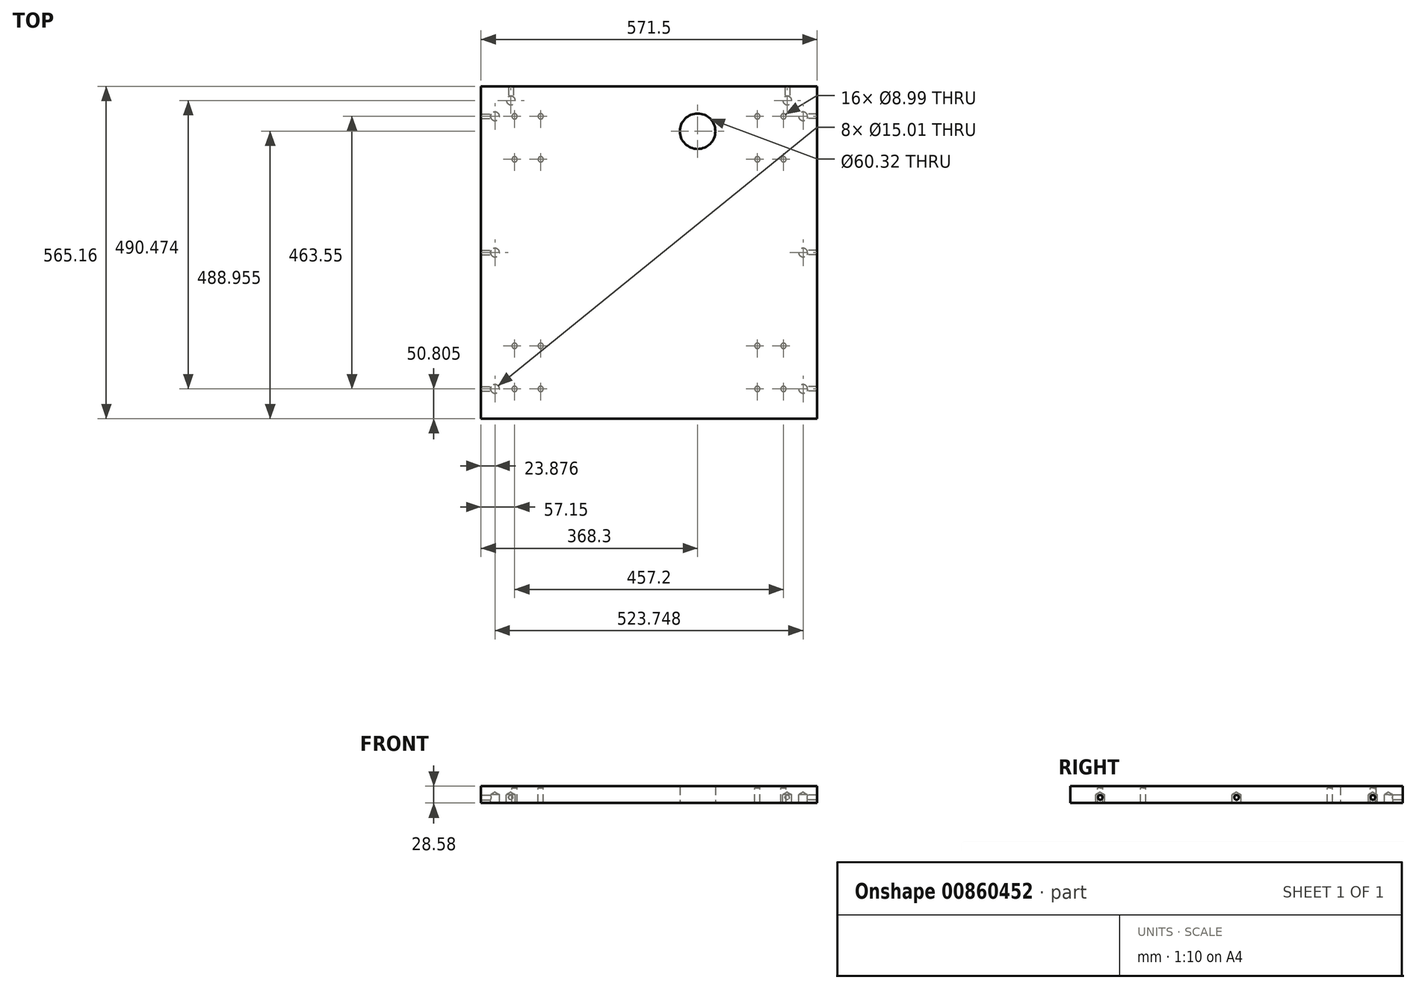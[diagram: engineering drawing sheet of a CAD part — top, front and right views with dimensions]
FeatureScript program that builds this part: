
annotation { "Feature Type Name" : "Feature", "Feature Type Description" : "" }
export const myFeature = defineFeature(function(context is Context, id is Id, definition is map)
    precondition{}
    {
        {
            var Q0;
            Q0=qCreatedBy(makeId("Top.planeOp"),FACE);
            var sketch = newSketch(context, id + "F0", { "sketchPlane" : qUnion([Q0])});
            skLineSegment(sketch, "E0.bottom", {"start": v(285.75, 282.58) * mm, "end": v(-285.75, 282.58) * mm});
            skLineSegment(sketch, "E0.top", {"start": v(285.75, -282.57) * mm, "end": v(-285.75, -282.58) * mm});
            skLineSegment(sketch, "E0.left", {"start": v(285.75, 282.58) * mm, "end": v(285.75, -282.57) * mm});
            skLineSegment(sketch, "E0.right", {"start": v(-285.75, 282.58) * mm, "end": v(-285.75, -282.58) * mm});
            skPoint(sketch, "E0.middle", {"position": v(0, 0) * mm});
            skCircle(sketch, "E1", {"center": v(82.55, 206.38) * mm, "radius": 30.16 * mm});
            skLineSegment(sketch, "E2", {"start": v(82.55, 206.38) * mm, "end": v(285.75, 206.38) * mm});
            skLineSegment(sketch, "E3", {"start": v(82.55, 206.38) * mm, "end": v(82.55, 282.58) * mm});
            skSolve(sketch);
        }
        {
            var Q0;
            Q0=makeQuery(id+"F0.imprint","IMPRINT",FACE,{"disambiguationData":[TD([[makeQuery(id+"F0.imprint","IMPRINT",EDGE,{"derivedFrom":sQuery(id+"F0.wireOp",EDGE,"E0.top")}),-1.0]])]});
            var Q1;
            {var subQ1=sQuery(id+"F0.wireOp",EDGE,"E0.left");var subQ7=sQuery(id+"F0.wireOp",EDGE,"E0.bottom");var subQ8=makeQuery(id+"F0.imprint","INTERSECT",VERTEX,{"derivedFrom":[subQ7,subQ1]});Q1=makeQuery(id+"F0.imprint","IMPRINT",FACE,{"disambiguationData":[TD([[makeQuery(id+"F0.imprint","IMPRINT",EDGE,{"disambiguationData":[TD([[subQ8,-1.0]])],"derivedFrom":subQ7}),1.0]])]});}
            extrude(context, id + "F1", {"entities" : qUnion([Q0, Q1]), "depth" : 28.57 * mm, "offsetDistance" : 25.4 * mm});
        }
        {
            var Q0;
            Q0=makeQuery(id+"F1.opExtrude","CAP_FACE",FACE,{"disambiguationData":[OSD([sQuery(id+"F0.wireOp",EDGE,"E0.bottom"),sQuery(id+"F0.wireOp",EDGE,"E0.top"),sQuery(id+"F0.wireOp",EDGE,"E0.left"),sQuery(id+"F0.wireOp",EDGE,"E0.right"),sQuery(id+"F0.wireOp",EDGE,"E1")])],"isStart":true});
            var sketch = newSketch(context, id + "F2", { "sketchPlane" : qUnion([Q0])});
            skLineSegment(sketch, "E4", {"start": v(-285.75, 282.58) * mm, "end": v(-261.87, 282.58) * mm});
            skLineSegment(sketch, "E5", {"start": v(-261.87, 282.58) * mm, "end": v(-261.87, 231.78) * mm});
            skLineSegment(sketch, "E6", {"start": v(-285.75, -282.57) * mm, "end": v(-261.87, -282.57) * mm});
            skLineSegment(sketch, "E7", {"start": v(-261.87, -282.57) * mm, "end": v(-261.87, -231.77) * mm});
            skLineSegment(sketch, "E8", {"start": v(-285.75, 0) * mm, "end": v(-261.87, 0) * mm});
            skLineSegment(sketch, "E9", {"start": v(285.75, 0) * mm, "end": v(261.87, 0) * mm});
            skLineSegment(sketch, "E10", {"start": v(285.75, 282.57) * mm, "end": v(261.87, 282.57) * mm});
            skLineSegment(sketch, "E11", {"start": v(261.87, 282.57) * mm, "end": v(261.87, 231.77) * mm});
            skLineSegment(sketch, "E12", {"start": v(285.75, -282.58) * mm, "end": v(261.87, -282.58) * mm});
            skLineSegment(sketch, "E13", {"start": v(261.87, -282.58) * mm, "end": v(261.87, -231.78) * mm});
            skPoint(sketch, "E14", {"position": v(-261.87, 231.78) * mm});
            skPoint(sketch, "E15", {"position": v(-261.87, 0) * mm});
            skPoint(sketch, "E16", {"position": v(-261.87, -231.77) * mm});
            skPoint(sketch, "E17", {"position": v(261.87, -231.78) * mm});
            skPoint(sketch, "E18", {"position": v(261.87, 0) * mm});
            skPoint(sketch, "E19", {"position": v(261.87, 231.77) * mm});
            skSolve(sketch);
        }
        {
            var Q0;
            Q0=sQuery(id+"F2.wireOp",VERTEX,"E14");
            var Q1;
            Q1=sQuery(id+"F2.wireOp",VERTEX,"E19");
            var Q2;
            Q2=sQuery(id+"F2.wireOp",VERTEX,"E15");
            var Q3;
            Q3=sQuery(id+"F2.wireOp",VERTEX,"E18");
            var Q4;
            Q4=sQuery(id+"F2.wireOp",VERTEX,"E17");
            var Q5;
            Q5=sQuery(id+"F2.wireOp",VERTEX,"E16");
            var Q6;
            Q6=makeQuery(id+"F1.opExtrude","SWEPT_BODY",BODY,{"disambiguationData":[OSD([sQuery(id+"F0.wireOp",EDGE,"E0.bottom"),sQuery(id+"F0.wireOp",EDGE,"E0.top"),sQuery(id+"F0.wireOp",EDGE,"E0.left"),sQuery(id+"F0.wireOp",EDGE,"E0.right"),sQuery(id+"F0.wireOp",EDGE,"E1")])]});
            hole(context, id + "F3", {"style" : HoleStyle.SIMPLE, "endStyle" : HoleEndStyle.BLIND, "holeDiameter" : 15 * mm, "majorDiameter" : 6.35 * mm, "holeDepth" : 14.22 * mm, "isTappedThrough" : true, "tappedDepth" : 12.7 * mm, "tapClearance" : 3, "locations" : qUnion([Q0, Q1, Q2, Q3, Q4, Q5]), "scope" : qUnion([Q6]), "startStyle" : HoleStartStyle.SKETCH});
        }
        {
            var Q0;
            Q0=makeQuery(id+"F1.opExtrude","SWEPT_FACE",FACE,{"disambiguationData":[OSD([sQuery(id+"F0.wireOp",EDGE,"E0.left")])]});
            var sketch = newSketch(context, id + "F4", { "sketchPlane" : qUnion([Q0])});
            skPoint(sketch, "E20", {"position": v(0, 9.52) * mm});
            skPoint(sketch, "E20.positionSnap0", {"position": v(0, 28.58) * mm});
            skPoint(sketch, "E21", {"position": v(-231.78, 9.53) * mm});
            skPoint(sketch, "E22", {"position": v(231.78, 9.52) * mm});
            skLineSegment(sketch, "E23", {"start": v(-231.78, 9.53) * mm, "end": v(-231.78, 0) * mm});
            skLineSegment(sketch, "E24", {"start": v(-282.58, 0) * mm, "end": v(-231.78, 0) * mm});
            skLineSegment(sketch, "E25", {"start": v(231.78, 9.52) * mm, "end": v(231.78, 0) * mm});
            skLineSegment(sketch, "E26", {"start": v(231.78, 0) * mm, "end": v(282.58, 0) * mm});
            skSolve(sketch);
        }
        {
            var Q0;
            Q0=sQuery(id+"F4.wireOp",VERTEX,"E21");
            var Q1;
            Q1=sQuery(id+"F4.wireOp",VERTEX,"E20");
            var Q2;
            Q2=sQuery(id+"F4.wireOp",VERTEX,"E22");
            var Q3;
            Q3=makeQuery(id+"F1.opExtrude","SWEPT_BODY",BODY,{"disambiguationData":[OSD([sQuery(id+"F0.wireOp",EDGE,"E0.bottom"),sQuery(id+"F0.wireOp",EDGE,"E0.top"),sQuery(id+"F0.wireOp",EDGE,"E0.left"),sQuery(id+"F0.wireOp",EDGE,"E0.right"),sQuery(id+"F0.wireOp",EDGE,"E1")])]});
            hole(context, id + "F5", {"style" : HoleStyle.SIMPLE, "endStyle" : HoleEndStyle.BLIND, "holeDiameter" : 8 * mm, "majorDiameter" : 6.35 * mm, "holeDepth" : 25.4 * mm, "isTappedThrough" : true, "tappedDepth" : 12.7 * mm, "tapClearance" : 3, "locations" : qUnion([Q0, Q1, Q2]), "scope" : qUnion([Q3]), "startStyle" : HoleStartStyle.SKETCH});
        }
        {
            var Q0;
            Q0=makeQuery(id+"F1.opExtrude","SWEPT_FACE",FACE,{"disambiguationData":[OSD([sQuery(id+"F0.wireOp",EDGE,"E0.right")])]});
            var sketch = newSketch(context, id + "F6", { "sketchPlane" : qUnion([Q0])});
            skPoint(sketch, "E27", {"position": v(-231.78, 9.53) * mm});
            skPoint(sketch, "E28", {"position": v(231.77, 9.52) * mm});
            skLineSegment(sketch, "E29", {"start": v(0, 0) * mm, "end": v(0, 9.53) * mm});
            skPoint(sketch, "E30", {"position": v(0, 9.53) * mm});
            skLineSegment(sketch, "E31", {"start": v(-231.78, 9.53) * mm, "end": v(-231.78, 0) * mm});
            skLineSegment(sketch, "E32", {"start": v(-231.78, 0) * mm, "end": v(-282.58, 0) * mm});
            skLineSegment(sketch, "E33", {"start": v(231.77, 9.52) * mm, "end": v(231.77, 0) * mm});
            skLineSegment(sketch, "E34", {"start": v(231.77, 0) * mm, "end": v(282.57, 0) * mm});
            skSolve(sketch);
        }
        {
            var Q0;
            Q0=sQuery(id+"F6.wireOp",VERTEX,"7JFDCdo1-Y3dr-wsHc-LP2G-7qkS5dpKQL4z.end");
            var Q1;
            Q1=sQuery(id+"F6.wireOp",VERTEX,"E30");
            var Q2;
            Q2=sQuery(id+"F6.wireOp",VERTEX,"E28");
            var Q3;
            Q3=sQuery(id+"F6.wireOp",VERTEX,"E27");
            var Q4;
            Q4=makeQuery(id+"F1.opExtrude","SWEPT_BODY",BODY,{"disambiguationData":[OSD([sQuery(id+"F0.wireOp",EDGE,"E0.bottom"),sQuery(id+"F0.wireOp",EDGE,"E0.top"),sQuery(id+"F0.wireOp",EDGE,"E0.left"),sQuery(id+"F0.wireOp",EDGE,"E0.right"),sQuery(id+"F0.wireOp",EDGE,"E1")])]});
            hole(context, id + "F7", {"style" : HoleStyle.SIMPLE, "endStyle" : HoleEndStyle.BLIND, "holeDiameter" : 8 * mm, "majorDiameter" : 6.35 * mm, "holeDepth" : 25.4 * mm, "isTappedThrough" : true, "tappedDepth" : 12.7 * mm, "tapClearance" : 3, "locations" : qUnion([Q0, Q1, Q2, Q3]), "scope" : qUnion([Q4]), "startStyle" : HoleStartStyle.SKETCH});
        }
        {
            var Q0;
            Q0=makeQuery(id+"F1.opExtrude","CAP_FACE",FACE,{"disambiguationData":[OSD([sQuery(id+"F0.wireOp",EDGE,"E0.bottom"),sQuery(id+"F0.wireOp",EDGE,"E0.top"),sQuery(id+"F0.wireOp",EDGE,"E0.left"),sQuery(id+"F0.wireOp",EDGE,"E0.right"),sQuery(id+"F0.wireOp",EDGE,"E1")])],"isStart":true});
            var sketch = newSketch(context, id + "F8", { "sketchPlane" : qUnion([Q0])});
            skLineSegment(sketch, "E35", {"start": v(-285.75, 282.58) * mm, "end": v(-228.6, 282.58) * mm});
            skLineSegment(sketch, "E36", {"start": v(-228.6, 282.58) * mm, "end": v(-228.6, 231.78) * mm});
            skLineSegment(sketch, "E37", {"start": v(285.75, 282.57) * mm, "end": v(228.6, 282.57) * mm});
            skLineSegment(sketch, "E38", {"start": v(228.6, 282.58) * mm, "end": v(228.6, 231.77) * mm});
            skLineSegment(sketch, "E39", {"start": v(-285.75, -282.57) * mm, "end": v(-228.6, -282.57) * mm});
            skLineSegment(sketch, "E40", {"start": v(-228.6, -282.57) * mm, "end": v(-228.6, -231.77) * mm});
            skLineSegment(sketch, "E41", {"start": v(285.75, -282.58) * mm, "end": v(228.6, -282.58) * mm});
            skLineSegment(sketch, "E42", {"start": v(228.6, -282.58) * mm, "end": v(228.6, -231.78) * mm});
            skPoint(sketch, "E43", {"position": v(-228.6, 231.78) * mm});
            skPoint(sketch, "E44", {"position": v(228.6, 231.77) * mm});
            skPoint(sketch, "E45", {"position": v(228.6, -231.78) * mm});
            skPoint(sketch, "E46", {"position": v(-228.6, -231.77) * mm});
            skLineSegment(sketch, "E47.bottom", {"start": v(-228.6, 231.78) * mm, "end": v(-184.15, 231.78) * mm});
            skLineSegment(sketch, "E47.top", {"start": v(-228.6, 158.62) * mm, "end": v(-184.15, 158.62) * mm});
            skLineSegment(sketch, "E47.left", {"start": v(-228.6, 231.78) * mm, "end": v(-228.6, 158.62) * mm});
            skLineSegment(sketch, "E47.right", {"start": v(-184.15, 231.78) * mm, "end": v(-184.15, 158.62) * mm});
            skLineSegment(sketch, "E48.bottom", {"start": v(228.6, 231.77) * mm, "end": v(184.15, 231.77) * mm});
            skLineSegment(sketch, "E48.top", {"start": v(228.6, 158.62) * mm, "end": v(184.15, 158.62) * mm});
            skLineSegment(sketch, "E48.left", {"start": v(228.6, 231.77) * mm, "end": v(228.6, 158.62) * mm});
            skLineSegment(sketch, "E48.right", {"start": v(184.15, 231.77) * mm, "end": v(184.15, 158.62) * mm});
            skLineSegment(sketch, "E49.bottom", {"start": v(228.6, -231.78) * mm, "end": v(184.15, -231.78) * mm});
            skLineSegment(sketch, "E49.top", {"start": v(228.6, -158.62) * mm, "end": v(184.15, -158.62) * mm});
            skLineSegment(sketch, "E49.left", {"start": v(228.6, -231.78) * mm, "end": v(228.6, -158.62) * mm});
            skLineSegment(sketch, "E49.right", {"start": v(184.15, -231.78) * mm, "end": v(184.15, -158.62) * mm});
            skLineSegment(sketch, "E50.bottom", {"start": v(-228.6, -231.77) * mm, "end": v(-184.15, -231.77) * mm});
            skLineSegment(sketch, "E50.top", {"start": v(-228.6, -158.62) * mm, "end": v(-184.15, -158.62) * mm});
            skLineSegment(sketch, "E50.left", {"start": v(-228.6, -231.77) * mm, "end": v(-228.6, -158.62) * mm});
            skLineSegment(sketch, "E50.right", {"start": v(-184.15, -231.77) * mm, "end": v(-184.15, -158.62) * mm});
            skPoint(sketch, "E51", {"position": v(-184.15, 231.78) * mm});
            skPoint(sketch, "E52", {"position": v(-228.6, 158.62) * mm});
            skPoint(sketch, "E53", {"position": v(-184.15, 158.62) * mm});
            skPoint(sketch, "E54", {"position": v(184.15, 231.77) * mm});
            skPoint(sketch, "E55", {"position": v(228.6, 158.62) * mm});
            skPoint(sketch, "E56", {"position": v(184.15, 158.62) * mm});
            skPoint(sketch, "E57", {"position": v(184.15, -158.62) * mm});
            skPoint(sketch, "E58", {"position": v(228.6, -158.62) * mm});
            skPoint(sketch, "E59", {"position": v(184.15, -231.78) * mm});
            skPoint(sketch, "E60", {"position": v(-184.15, -231.77) * mm});
            skPoint(sketch, "E61", {"position": v(-184.15, -158.62) * mm});
            skPoint(sketch, "E62", {"position": v(-228.6, -158.62) * mm});
            skSolve(sketch);
        }
        {
            var Q0;
            Q0=sQuery(id+"F8.wireOp",VERTEX,"E46");
            var Q1;
            Q1=sQuery(id+"F8.wireOp",VERTEX,"E60");
            var Q2;
            Q2=sQuery(id+"F8.wireOp",VERTEX,"E61");
            var Q3;
            Q3=sQuery(id+"F8.wireOp",VERTEX,"E62");
            var Q4;
            Q4=sQuery(id+"F8.wireOp",VERTEX,"E52");
            var Q5;
            Q5=sQuery(id+"F8.wireOp",VERTEX,"E43");
            var Q6;
            Q6=sQuery(id+"F8.wireOp",VERTEX,"E51");
            var Q7;
            Q7=sQuery(id+"F8.wireOp",VERTEX,"E53");
            var Q8;
            Q8=sQuery(id+"F8.wireOp",VERTEX,"E54");
            var Q9;
            Q9=sQuery(id+"F8.wireOp",VERTEX,"E44");
            var Q10;
            Q10=sQuery(id+"F8.wireOp",VERTEX,"E55");
            var Q11;
            Q11=sQuery(id+"F8.wireOp",VERTEX,"E56");
            var Q12;
            Q12=sQuery(id+"F8.wireOp",VERTEX,"E57");
            var Q13;
            Q13=sQuery(id+"F8.wireOp",VERTEX,"E58");
            var Q14;
            Q14=sQuery(id+"F8.wireOp",VERTEX,"E45");
            var Q15;
            Q15=sQuery(id+"F8.wireOp",VERTEX,"E59");
            var Q16;
            Q16=makeQuery(id+"F1.opExtrude","SWEPT_BODY",BODY,{"disambiguationData":[OSD([sQuery(id+"F0.wireOp",EDGE,"E0.bottom"),sQuery(id+"F0.wireOp",EDGE,"E0.top"),sQuery(id+"F0.wireOp",EDGE,"E0.left"),sQuery(id+"F0.wireOp",EDGE,"E0.right"),sQuery(id+"F0.wireOp",EDGE,"E1")])]});
            hole(context, id + "F9", {"style" : HoleStyle.SIMPLE, "endStyle" : HoleEndStyle.BLIND, "holeDiameter" : 9 * mm, "majorDiameter" : 6.35 * mm, "holeDepth" : 25.4 * mm, "isTappedThrough" : true, "tappedDepth" : 12.7 * mm, "tapClearance" : 3, "locations" : qUnion([Q0, Q1, Q2, Q3, Q4, Q5, Q6, Q7, Q8, Q9, Q10, Q11, Q12, Q13, Q14, Q15]), "scope" : qUnion([Q16]), "startStyle" : HoleStartStyle.SKETCH});
        }
        {
            var Q0;
            Q0=makeQuery(id+"F1.opExtrude","CAP_FACE",FACE,{"disambiguationData":[OSD([sQuery(id+"F0.wireOp",EDGE,"E0.bottom"),sQuery(id+"F0.wireOp",EDGE,"E0.top"),sQuery(id+"F0.wireOp",EDGE,"E0.left"),sQuery(id+"F0.wireOp",EDGE,"E0.right"),sQuery(id+"F0.wireOp",EDGE,"E1")])],"isStart":true});
            var sketch = newSketch(context, id + "F10", { "sketchPlane" : qUnion([Q0])});
            skLineSegment(sketch, "E63", {"start": v(-285.75, -282.57) * mm, "end": v(-234.95, -282.57) * mm});
            skLineSegment(sketch, "E64", {"start": v(-234.95, -282.57) * mm, "end": v(-234.95, -258.7) * mm});
            skLineSegment(sketch, "E65", {"start": v(285.75, -282.58) * mm, "end": v(234.95, -282.58) * mm});
            skLineSegment(sketch, "E66", {"start": v(234.95, -282.58) * mm, "end": v(234.95, -258.7) * mm});
            skPoint(sketch, "E67", {"position": v(-234.95, -258.7) * mm});
            skPoint(sketch, "E68", {"position": v(234.95, -258.7) * mm});
            skSolve(sketch);
        }
        {
            var Q0;
            Q0=sQuery(id+"F10.wireOp",VERTEX,"E67");
            var Q1;
            Q1=sQuery(id+"F10.wireOp",VERTEX,"E68");
            var Q2;
            Q2=makeQuery(id+"F1.opExtrude","SWEPT_BODY",BODY,{"disambiguationData":[OSD([sQuery(id+"F0.wireOp",EDGE,"E0.bottom"),sQuery(id+"F0.wireOp",EDGE,"E0.top"),sQuery(id+"F0.wireOp",EDGE,"E0.left"),sQuery(id+"F0.wireOp",EDGE,"E0.right"),sQuery(id+"F0.wireOp",EDGE,"E1")])]});
            hole(context, id + "F11", {"style" : HoleStyle.SIMPLE, "endStyle" : HoleEndStyle.BLIND, "holeDiameter" : 15 * mm, "majorDiameter" : 6.35 * mm, "holeDepth" : 14.22 * mm, "isTappedThrough" : true, "tappedDepth" : 12.7 * mm, "tapClearance" : 3, "locations" : qUnion([Q0, Q1]), "scope" : qUnion([Q2]), "startStyle" : HoleStartStyle.SKETCH});
        }
        {
            var Q0;
            Q0=makeQuery(id+"F1.opExtrude","SWEPT_FACE",FACE,{"disambiguationData":[OSD([sQuery(id+"F0.wireOp",EDGE,"E0.bottom")])]});
            var sketch = newSketch(context, id + "F12", { "sketchPlane" : qUnion([Q0])});
            skLineSegment(sketch, "E69", {"start": v(-285.75, 0) * mm, "end": v(-285.75, 9.53) * mm});
            skLineSegment(sketch, "E70", {"start": v(-285.75, 9.53) * mm, "end": v(-234.95, 9.53) * mm});
            skLineSegment(sketch, "E71", {"start": v(285.75, 0) * mm, "end": v(285.75, 9.53) * mm});
            skLineSegment(sketch, "E72", {"start": v(285.75, 9.53) * mm, "end": v(234.95, 9.53) * mm});
            skPoint(sketch, "E73", {"position": v(-234.95, 9.53) * mm});
            skPoint(sketch, "E74", {"position": v(234.95, 9.53) * mm});
            skSolve(sketch);
        }
        {
            var Q0;
            Q0=sQuery(id+"F12.wireOp",VERTEX,"E70.end");
            var Q1;
            Q1=sQuery(id+"F12.wireOp",VERTEX,"E74");
            var Q2;
            Q2=makeQuery(id+"F1.opExtrude","SWEPT_BODY",BODY,{"disambiguationData":[OSD([sQuery(id+"F0.wireOp",EDGE,"E0.bottom"),sQuery(id+"F0.wireOp",EDGE,"E0.top"),sQuery(id+"F0.wireOp",EDGE,"E0.left"),sQuery(id+"F0.wireOp",EDGE,"E0.right"),sQuery(id+"F0.wireOp",EDGE,"E1")])]});
            hole(context, id + "F13", {"style" : HoleStyle.SIMPLE, "endStyle" : HoleEndStyle.BLIND, "holeDiameter" : 8 * mm, "majorDiameter" : 6.35 * mm, "holeDepth" : 25.4 * mm, "isTappedThrough" : true, "tappedDepth" : 12.7 * mm, "tapClearance" : 3, "locations" : qUnion([Q0, Q1]), "scope" : qUnion([Q2]), "startStyle" : HoleStartStyle.SKETCH});
        }
    });
